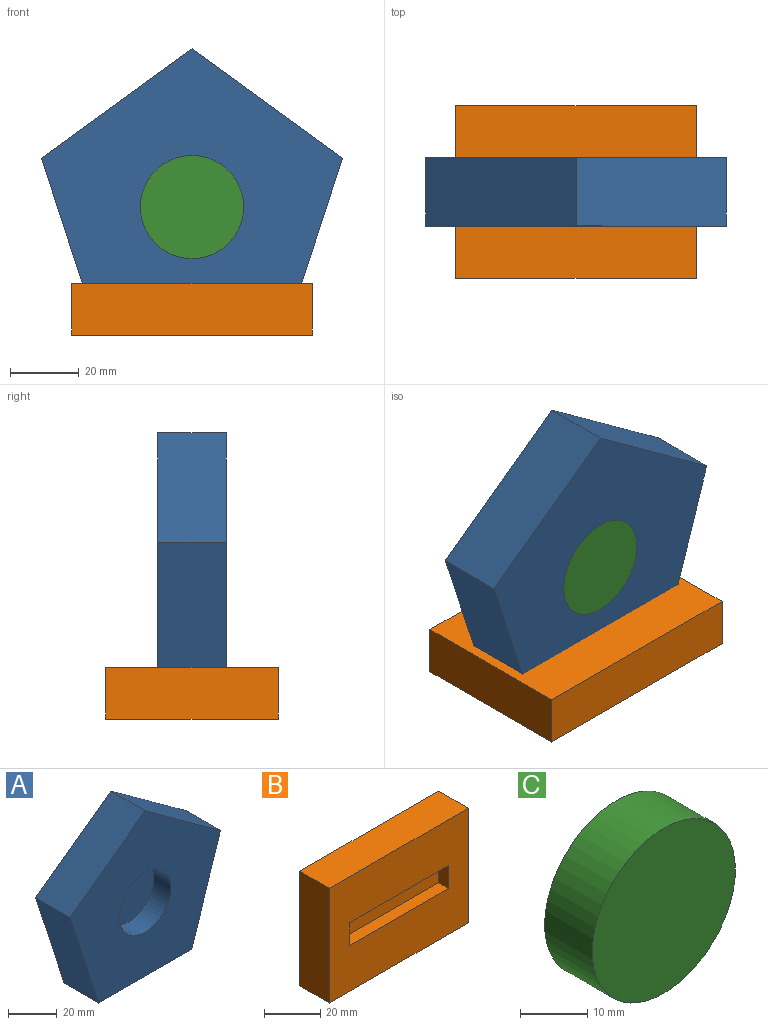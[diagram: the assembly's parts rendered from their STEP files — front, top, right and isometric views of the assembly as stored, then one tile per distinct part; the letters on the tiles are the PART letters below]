
ASSEMBLY  parts=3 mates=2
PART A: 9 faces, bbox 87.4x20x83.1 mm
  f0: plane 51.38x20mm, normal (0.95,0,-0.31), area 1080.4mm2, adj f1,f4,f5,f6
  f1: plane 43.7x31.75mm, normal (0.59,0,0.81), area 1080.4mm2, adj f0,f2,f5,f6
  f2: plane 43.7x31.75mm, normal (-0.59,0,0.81), area 1080.4mm2, adj f1,f3,f5,f6
  f3: plane 51.38x20mm, normal (-0.95,0,-0.31), area 1080.4mm2, adj f2,f4,f5,f6
  f4: plane 54.02x20mm, normal (0,0,-1), area 1080.4mm2, adj f0,f3,f5,f6
  f5: plane 87.41x83.13mm, normal (0,-1,0), area 4313.8mm2, adj f0,f1,f2,f3,f4,f7
  f6: plane 87.41x83.13mm, normal (0,1,0), area 5020.7mm2, adj f0,f1,f2,f3,f4
  f7: cylinder r=15mm len=30mm, axis (0,-1,0), area 942.5mm2, adj f5,f8
  f8: plane 30x30mm, normal (0,-1,0), area 706.9mm2, adj f7
PART B: 11 faces, bbox 70x15x50 mm
  f0: plane 70x50mm, normal (0,-1,0), area 3000mm2, adj f1,f2,f3,f4,f6,f7,f8,f9
  f1: plane 70x15mm, normal (0,0,1), area 1050mm2, adj f0,f2,f4,f5
  f2: plane 50x15mm, normal (-1,0,0), area 750mm2, adj f0,f1,f3,f5
  f3: plane 70x15mm, normal (0,0,-1), area 1050mm2, adj f0,f2,f4,f5
  f4: plane 50x15mm, normal (1,0,0), area 750mm2, adj f0,f1,f3,f5
  f5: plane 70x50mm, normal (0,1,0), area 3500mm2, adj f1,f2,f3,f4
  f6: plane 50x5mm, normal (0,0,-1), area 250mm2, adj f0,f7,f9,f10
  f7: plane 10x5mm, normal (1,0,0), area 50mm2, adj f0,f6,f8,f10
  f8: plane 50x5mm, normal (0,0,1), area 250mm2, adj f0,f7,f9,f10
  f9: plane 10x5mm, normal (-1,0,0), area 50mm2, adj f0,f6,f8,f10
  f10: plane 50x10mm, normal (0,-1,0), area 500mm2, adj f6,f7,f8,f9
PART C: 3 faces, bbox 30x10x30 mm
  f0: cylinder r=15mm len=30mm, axis (0,1,0), area 942.5mm2, adj f1,f2
  f1: plane 30x30mm, normal (0,-1,0), area 706.9mm2, adj f0
  f2: plane 30x30mm, normal (0,1,0), area 706.9mm2, adj f0
PLACE A t=(47.72,25.89,-21.87)mm
PLACE B rot(axis=(1,0,0),90deg) t=(47.72,15.89,-44.05)mm
PLACE C t=(47.72,15.89,-21.87)mm
MATE fastened B.f0 <-> A.f4  axis (0,0,-1) through (47.72,15.89,-59.05)mm
MATE fastened C.f0 <-> A.f7  axis (0,-1,0) through (47.72,5.89,-21.87)mm
